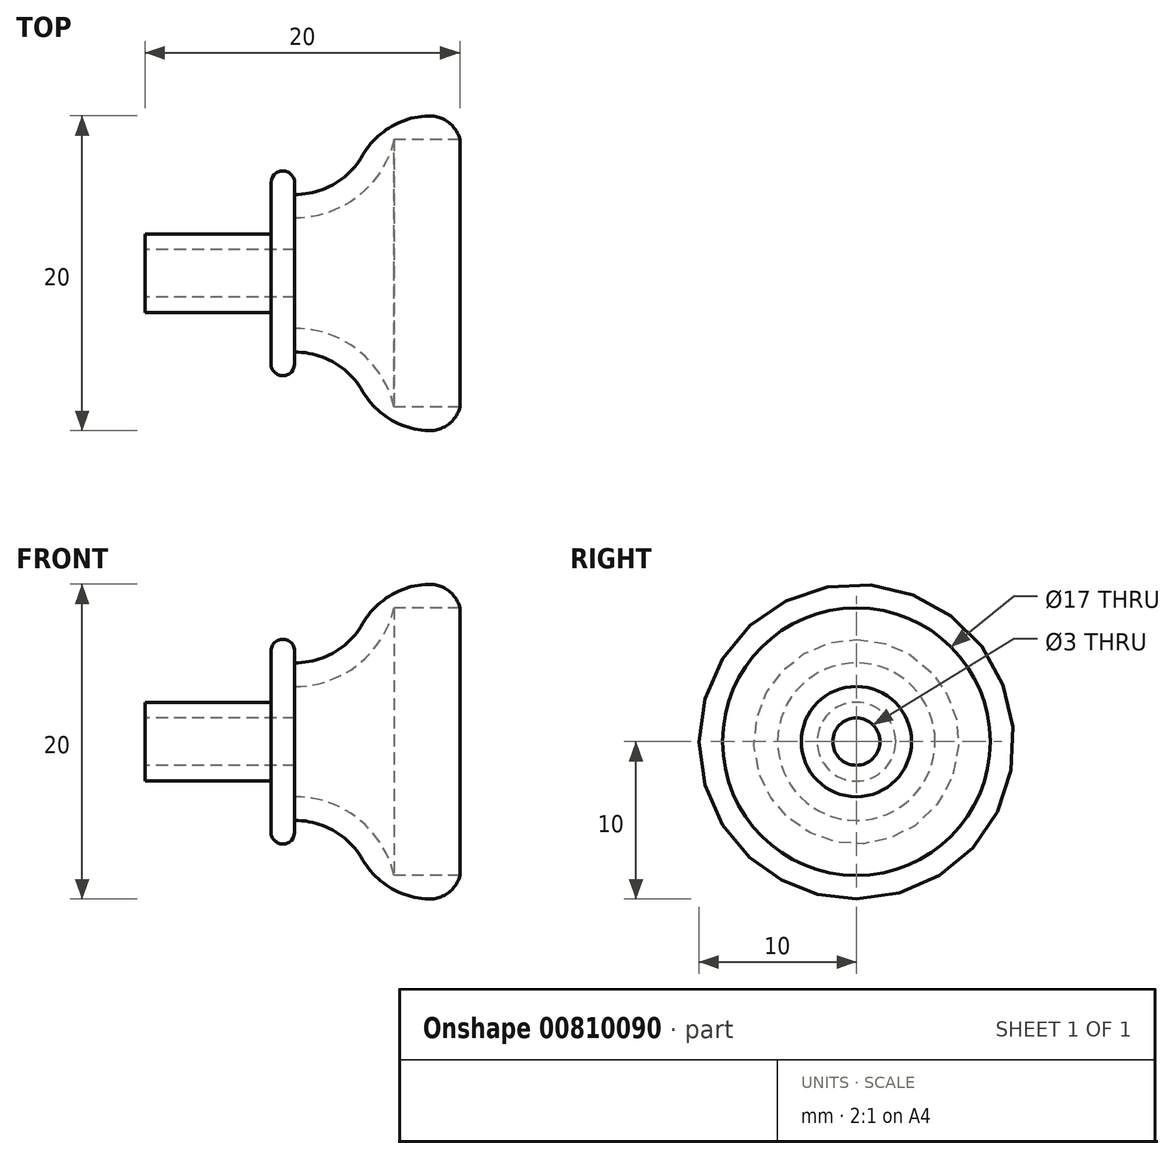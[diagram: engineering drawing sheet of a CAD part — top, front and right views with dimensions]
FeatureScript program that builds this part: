
annotation { "Feature Type Name" : "Feature", "Feature Type Description" : "" }
export const myFeature = defineFeature(function(context is Context, id is Id, definition is map)
    precondition{}
    {
        {
            var Q0;
            Q0=qCreatedBy(makeId("Top.planeOp"),FACE);
            var sketch = newSketch(context, id + "F0", { "sketchPlane" : qUnion([Q0])});
            skLineSegment(sketch, "E0.left", {"start": v(0, 0) * mm, "end": v(0, 2.5) * mm});
            skPoint(sketch, "E1", {"position": v(8, 2.5) * mm});
            skLineSegment(sketch, "E2", {"start": v(0, 2.5) * mm, "end": v(0, 2.5) * mm});
            skArc(sketch, "E3", {"start": v(8, 5.75) * mm, "mid": v(8.75, 6.5) * mm, "end": v(9.5, 5.75) * mm});
            skPoint(sketch, "E4", {"position": v(0, 2.5) * mm});
            skArc(sketch, "E5", {"start": v(9.5, 5) * mm, "mid": v(13.04, 6.46) * mm, "end": v(14.5, 10) * mm});
            skLineSegment(sketch, "E6.left", {"start": v(8, 5.75) * mm, "end": v(8, 2.5) * mm});
            skLineSegment(sketch, "E7", {"start": v(0, 2.5) * mm, "end": v(8, 2.5) * mm});
            skLineSegment(sketch, "E8", {"start": v(9.5, 5.75) * mm, "end": v(9.5, 5) * mm});
            skLineSegment(sketch, "E9", {"start": v(14.5, 10) * mm, "end": v(20, 10) * mm});
            skLineSegment(sketch, "E10", {"start": v(9.5, 3.5) * mm, "end": v(9.5, 0) * mm});
            skLineSegment(sketch, "E11", {"start": v(20, 10) * mm, "end": v(20, 8.5) * mm});
            skLineSegment(sketch, "E12", {"start": v(0, 0) * mm, "end": v(9.5, 0) * mm});
            skPoint(sketch, "E13", {"position": v(15.82, 8.5) * mm});
            skArc(sketch, "E14", {"start": v(15.82, 8.5) * mm, "mid": v(13.53, 4.9) * mm, "end": v(9.5, 3.5) * mm});
            skLineSegment(sketch, "E15", {"start": v(15.82, 8.5) * mm, "end": v(20, 8.5) * mm});
            skSolve(sketch);
        }
        {
            var Q0;
            Q0=makeQuery(id+"F0.imprint","IMPRINT",FACE,{"disambiguationData":[TD([[makeQuery(id+"F0.imprint","IMPRINT",EDGE,{"derivedFrom":sQuery(id+"F0.wireOp",EDGE,"E0.bottom")}),1.0]])]});
            var Q1;
            Q1=makeQuery(id+"F0.imprint","IMPRINT",FACE,{"disambiguationData":[TD([[makeQuery(id+"F0.imprint","IMPRINT",EDGE,{"derivedFrom":sQuery(id+"F0.wireOp",EDGE,"E0.left")}),-1.0]])]});
            var Q2;
            Q2=sQuery(id+"F0.wireOp",EDGE,"E12");
            revolve(context, id + "F1", {"surfaceOperationType" : NewSurfaceOperationType.NEW, "entities" : qUnion([Q0, Q1]), "axis" : qUnion([Q2]), "revolveType" : RevolveType.FULL});
        }
        {
            var Q0;
            Q0=qCreatedBy(makeId("Right.planeOp"),FACE);
            var sketch = newSketch(context, id + "F2", { "sketchPlane" : qUnion([Q0])});
            skPoint(sketch, "E16", {"position": v(0, 0) * mm});
            skSolve(sketch);
        }
        {
            var Q0;
            Q0=sQuery(id+"F2.wireOp",VERTEX,"E16");
            var Q1;
            Q1=makeQuery(id+"F1.opRevolve","SWEPT_BODY",BODY,{"disambiguationData":[OSD([sQuery(id+"F0.wireOp",EDGE,"E0.bottom"),sQuery(id+"F0.wireOp",EDGE,"E0.left"),sQuery(id+"F0.wireOp",EDGE,"E3"),sQuery(id+"F0.wireOp",EDGE,"E5"),sQuery(id+"F0.wireOp",EDGE,"E6.left"),sQuery(id+"F0.wireOp",EDGE,"E7"),sQuery(id+"F0.wireOp",EDGE,"E8"),sQuery(id+"F0.wireOp",EDGE,"E9"),sQuery(id+"F0.wireOp",EDGE,"spAbJsco-E1Te-LGE2-DCND-xSgtzWXDVyto")])]});
            hole(context, id + "F3", {"style" : HoleStyle.SIMPLE, "endStyle" : HoleEndStyle.BLIND, "oppositeDirection" : true, "holeDiameter" : 3 * mm, "majorDiameter" : 5 * mm, "holeDepth" : 40 * mm, "isTappedThrough" : true, "tappedDepth" : 12 * mm, "tapClearance" : 3, "locations" : qUnion([Q0]), "scope" : qUnion([Q1])});
        }
        {
            var Q0;
            Q0=makeQuery(id+"F1.opRevolve","SWEPT_EDGE",EDGE,{"disambiguationData":[OSD([sQuery(id+"F0.wireOp",EDGE,"E5"),sQuery(id+"F0.wireOp",EDGE,"E9")])]});
            fillet(context, id + "F4", {"entities" : qUnion([Q0]), "radius" : 5 * mm, "tangentPropagation" : true, "allowEdgeOverflow" : false});
        }
        {
            var Q0;
            Q0=makeQuery(id+"F1.opRevolve","SWEPT_EDGE",EDGE,{"disambiguationData":[OSD([sQuery(id+"F0.wireOp",EDGE,"E9"),sQuery(id+"F0.wireOp",EDGE,"spAbJsco-E1Te-LGE2-DCND-xSgtzWXDVyto")])]});
            fillet(context, id + "F5", {"entities" : qUnion([Q0]), "radius" : 2 * mm, "tangentPropagation" : true, "allowEdgeOverflow" : false});
        }
    });
